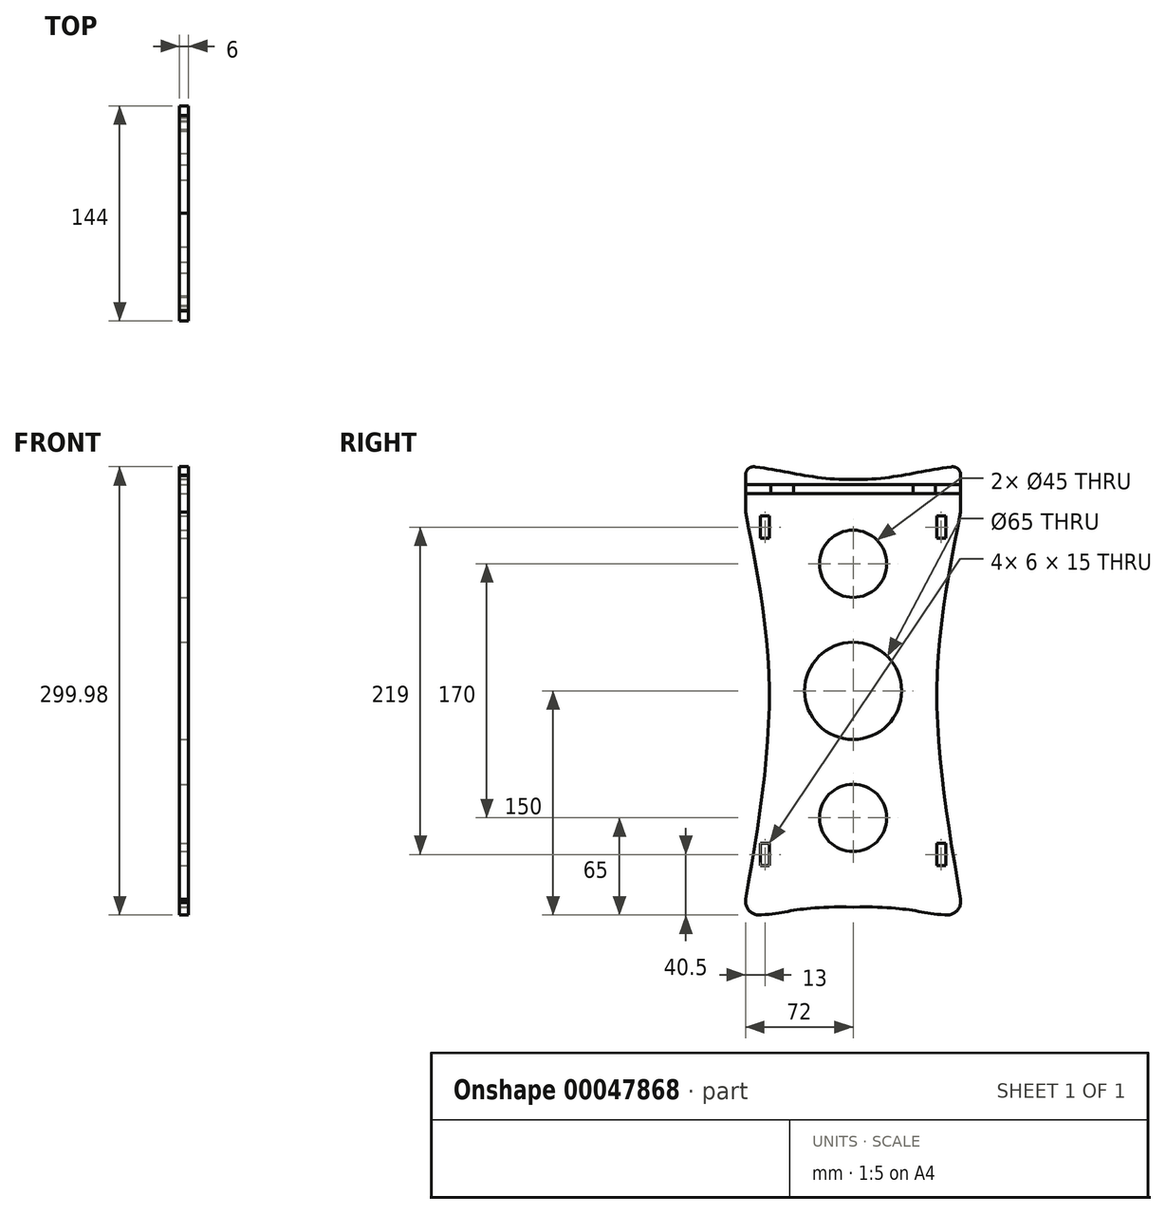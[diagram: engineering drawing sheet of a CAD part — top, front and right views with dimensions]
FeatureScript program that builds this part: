
annotation { "Feature Type Name" : "Feature", "Feature Type Description" : "" }
export const myFeature = defineFeature(function(context is Context, id is Id, definition is map)
    precondition{}
    {
        {
            var Q0;
            Q0=qCreatedBy(makeId("Right.planeOp"),FACE);
            var sketch = newSketch(context, id + "F0", { "sketchPlane" : qUnion([Q0])});
            skLineSegment(sketch, "E0.rect.bottom", {"start": v(-72, 150) * mm, "end": v(72, 150) * mm});
            skLineSegment(sketch, "E0.rect.top", {"start": v(-72, -150) * mm, "end": v(72, -150) * mm});
            skLineSegment(sketch, "E0.rect.left", {"start": v(-72, 150) * mm, "end": v(-72, -150) * mm});
            skLineSegment(sketch, "E0.rect.right", {"start": v(72, 150) * mm, "end": v(72, -150) * mm});
            skPoint(sketch, "E0.rect.middle", {"position": v(0, 0) * mm});
            skSolve(sketch);
        }
        {
            var Q0;
            Q0 = qSketchRegion(id + "F0", true);
            extrude(context, id + "F1", {"entities" : qUnion([Q0]), "depth" : 6 * mm});
        }
        {
            var Q0;
            Q0=makeQuery(id+"F1.opExtrude","CAP_FACE",FACE,{"disambiguationData":[OSD([sQuery(id+"F0.wireOp",EDGE,"E0.rect.bottom"),sQuery(id+"F0.wireOp",EDGE,"E0.rect.top"),sQuery(id+"F0.wireOp",EDGE,"E0.rect.left"),sQuery(id+"F0.wireOp",EDGE,"E0.rect.right")])],"isStart":false});
            var sketch = newSketch(context, id + "F2", { "sketchPlane" : qUnion([Q0])});
            skLineSegment(sketch, "E1", {"start": v(0, 150) * mm, "end": v(0, 138) * mm, "construction": true});
            skLineSegment(sketch, "E2", {"start": v(0, 138) * mm, "end": v(0, 135) * mm});
            skLineSegment(sketch, "E3.rect.bottom", {"start": v(75, 132) * mm, "end": v(-75, 132) * mm});
            skLineSegment(sketch, "E3.rect.top", {"start": v(75, 138) * mm, "end": v(-75, 138) * mm});
            skLineSegment(sketch, "E3.rect.left", {"start": v(75, 132) * mm, "end": v(75, 138) * mm});
            skLineSegment(sketch, "E3.rect.right", {"start": v(-75, 132) * mm, "end": v(-75, 138) * mm});
            skPoint(sketch, "E3.rect.middle", {"position": v(0, 135) * mm});
            skSolve(sketch);
        }
        {
            var Q0;
            Q0 = qSketchRegion(id + "F2", true);
            extrude(context, id + "F3", {"entities" : qUnion([Q0]), "operationType" : NewBodyOperationType.REMOVE, "oppositeDirection" : true, "depth" : 0.1 * mm});
        }
        {
            var Q0;
            {var subQ0=sQuery(id+"F0.wireOp",EDGE,"E0.rect.top");var subQ1=sQuery(id+"F0.wireOp",EDGE,"E0.rect.left");var subQ2=sQuery(id+"F0.wireOp",EDGE,"E0.rect.right");Q0=makeQuery(id+"F3.boolean.opBoolean","SPLIT",FACE,{"disambiguationData":[TD([makeQuery(id+"F1.opExtrude","SWEPT_FACE",FACE,{"disambiguationData":[OSD([subQ0])]})])],"derivedFrom":makeQuery(id+"F1.opExtrude","CAP_FACE",FACE,{"disambiguationData":[OSD([sQuery(id+"F0.wireOp",EDGE,"E0.rect.bottom"),subQ0,subQ1,subQ2])],"isStart":false})});}
            var sketch = newSketch(context, id + "F4", { "sketchPlane" : qUnion([Q0])});
            skArc(sketch, "E4", {"start": v(-72, -139.62) * mm, "mid": v(-69.27, -147.38) * mm, "end": v(-61.48, -150) * mm});
            skPoint(sketch, "E4.first.point", {"position": v(-61.48, -150) * mm});
            skPoint(sketch, "E4.second.point", {"position": v(-72, -139.62) * mm});
            skFitSpline(sketch, "E5", {"points": [v(-72, 119.57) * mm, v(-56.11, 0) * mm, v(-72, -139.62) * mm], "startDerivative": vector(48.35, -243.74) * mm, "endDerivative": vector(-47.13, -274.25) * mm});
            skLineSegment(sketch, "E6", {"start": v(0, -150) * mm, "end": v(0, -144.73) * mm, "construction": true});
            skPoint(sketch, "E6.endSnap0", {"position": v(0, -150) * mm});
            skFitSpline(sketch, "E7", {"points": [v(0, -144.73) * mm, v(-61.48, -150) * mm], "startDerivative": vector(-108.63, 2.12) * mm, "endDerivative": vector(-61.48, -5.27) * mm});
            skLineSegment(sketch, "E8", {"start": v(0, 150.81) * mm, "end": v(0, 141.49) * mm, "construction": true});
            skArc(sketch, "E9", {"start": v(-65.4, 149.82) * mm, "mid": v(-70.1, 148.72) * mm, "end": v(-71.9, 144.26) * mm});
            skLineSegment(sketch, "E10", {"start": v(-72, 119.57) * mm, "end": v(-83.4, 131.88) * mm});
            skLineSegment(sketch, "E11", {"start": v(-83.4, 131.88) * mm, "end": v(-71.9, 144.26) * mm});
            skFitSpline(sketch, "E12", {"points": [v(-65.4, 149.82) * mm, v(0, 141.49) * mm], "startDerivative": vector(66.6, -8.49) * mm, "endDerivative": vector(75.41, 1.56) * mm});
            skFitSpline(sketch, "E13.MirrorCS", {"points": [v(65.4, 149.82) * mm, v(0, 141.49) * mm], "startDerivative": vector(-66.6, -8.49) * mm, "endDerivative": vector(-75.41, 1.56) * mm});
            skArc(sketch, "E14.MirrorCS", {"start": v(65.4, 149.82) * mm, "mid": v(70.1, 148.72) * mm, "end": v(71.9, 144.26) * mm});
            skLineSegment(sketch, "E15.MirrorCS", {"start": v(83.4, 131.88) * mm, "end": v(71.9, 144.26) * mm});
            skLineSegment(sketch, "E16.MirrorCS", {"start": v(72, 119.57) * mm, "end": v(83.4, 131.88) * mm});
            skFitSpline(sketch, "E17.MirrorCS", {"points": [v(72, 119.57) * mm, v(56.11, 0) * mm, v(72, -139.62) * mm], "startDerivative": vector(-48.35, -243.74) * mm, "endDerivative": vector(47.13, -274.25) * mm});
            skArc(sketch, "E18.MirrorCS", {"start": v(72, -139.62) * mm, "mid": v(69.27, -147.38) * mm, "end": v(61.48, -150) * mm});
            skFitSpline(sketch, "E19.MirrorCS", {"points": [v(0, -144.73) * mm, v(61.48, -150) * mm], "startDerivative": vector(108.63, 2.12) * mm, "endDerivative": vector(61.48, -5.27) * mm});
            skLineSegment(sketch, "E20", {"start": v(0, 141.49) * mm, "end": v(0, -144.73) * mm, "construction": true});
            skCircle(sketch, "E21", {"center": v(0, 85) * mm, "radius": 22.5 * mm});
            skCircle(sketch, "E22.MirrorC", {"center": v(0, -85) * mm, "radius": 22.5 * mm});
            skCircle(sketch, "E23", {"center": v(0, 0) * mm, "radius": 32.5 * mm});
            skSolve(sketch);
        }
        {
            var Q0;
            Q0 = qSketchRegion(id + "F4", true);
            extrude(context, id + "F5", {"entities" : qUnion([Q0]), "operationType" : NewBodyOperationType.INTERSECT, "oppositeDirection" : true, "depth" : 25 * mm});
        }
        {
            var Q0;
            Q0=makeQuery(id+"F3.boolean.opBoolean","COPY",FACE,{"derivedFrom":makeQuery(id+"F3.opExtrude","CAP_FACE",FACE,{"disambiguationData":[OSD([sQuery(id+"F2.wireOp",EDGE,"E3.rect.bottom"),sQuery(id+"F2.wireOp",EDGE,"E3.rect.top"),sQuery(id+"F2.wireOp",EDGE,"E3.rect.left"),sQuery(id+"F2.wireOp",EDGE,"E3.rect.right")])],"isStart":false})});
            var sketch = newSketch(context, id + "F6", { "sketchPlane" : qUnion([Q0])});
            skLineSegment(sketch, "E24", {"start": v(0, 132) * mm, "end": v(0, 123.5) * mm, "construction": true});
            skPoint(sketch, "E24.endSnap0", {"position": v(0, 132) * mm});
            skLineSegment(sketch, "E25.bottom", {"start": v(-55, 138) * mm, "end": v(-40, 138) * mm});
            skLineSegment(sketch, "E25.top", {"start": v(-55, 132) * mm, "end": v(-40, 132) * mm});
            skLineSegment(sketch, "E25.left", {"start": v(-55, 138) * mm, "end": v(-55, 132) * mm});
            skLineSegment(sketch, "E25.right", {"start": v(-40, 138) * mm, "end": v(-40, 132) * mm});
            skLineSegment(sketch, "E26.MirrorCS", {"start": v(55, 138) * mm, "end": v(40, 138) * mm});
            skLineSegment(sketch, "E27.MirrorCS", {"start": v(40, 138) * mm, "end": v(40, 132) * mm});
            skLineSegment(sketch, "E28.MirrorCS", {"start": v(55, 132) * mm, "end": v(40, 132) * mm});
            skLineSegment(sketch, "E29.MirrorCS", {"start": v(55, 138) * mm, "end": v(55, 132) * mm});
            skSolve(sketch);
        }
        {
            var Q0;
            Q0 = qSketchRegion(id + "F6", true);
            extrude(context, id + "F7", {"entities" : qUnion([Q0]), "operationType" : NewBodyOperationType.REMOVE, "oppositeDirection" : true, "depth" : 25 * mm});
        }
        {
            var Q0;
            {var subQ0=sQuery(id+"F0.wireOp",EDGE,"E0.rect.top");var subQ1=sQuery(id+"F0.wireOp",EDGE,"E0.rect.left");var subQ2=sQuery(id+"F0.wireOp",EDGE,"E0.rect.right");Q0=makeQuery(id+"F3.boolean.opBoolean","SPLIT",FACE,{"disambiguationData":[TD([makeQuery(id+"F1.opExtrude","SWEPT_FACE",FACE,{"disambiguationData":[OSD([subQ0])]})])],"derivedFrom":makeQuery(id+"F1.opExtrude","CAP_FACE",FACE,{"disambiguationData":[OSD([sQuery(id+"F0.wireOp",EDGE,"E0.rect.bottom"),subQ0,subQ1,subQ2])],"isStart":false})});}
            var sketch = newSketch(context, id + "F8", { "sketchPlane" : qUnion([Q0])});
            skLineSegment(sketch, "E30.bottom", {"start": v(44.43, 137.81) * mm, "end": v(50.43, 137.81) * mm, "construction": true});
            skLineSegment(sketch, "E30.top", {"start": v(44.43, 112.81) * mm, "end": v(50.43, 112.81) * mm, "construction": true});
            skLineSegment(sketch, "E30.left", {"start": v(44.43, 137.81) * mm, "end": v(44.43, 112.81) * mm, "construction": true});
            skLineSegment(sketch, "E30.right", {"start": v(50.43, 137.81) * mm, "end": v(50.43, 112.81) * mm, "construction": true});
            skLineSegment(sketch, "E31.bottom", {"start": v(56, 117) * mm, "end": v(62, 117) * mm});
            skLineSegment(sketch, "E31.top", {"start": v(56, 102) * mm, "end": v(62, 102) * mm});
            skLineSegment(sketch, "E31.left", {"start": v(56, 117) * mm, "end": v(56, 102) * mm});
            skLineSegment(sketch, "E31.right", {"start": v(62, 117) * mm, "end": v(62, 102) * mm});
            skLineSegment(sketch, "E32.MirrorCS", {"start": v(56, -117) * mm, "end": v(56, -102) * mm});
            skLineSegment(sketch, "E33.MirrorCS", {"start": v(56, -117) * mm, "end": v(62, -117) * mm});
            skLineSegment(sketch, "E34.MirrorCS", {"start": v(62, -117) * mm, "end": v(62, -102) * mm});
            skLineSegment(sketch, "E35.MirrorCS", {"start": v(56, -102) * mm, "end": v(62, -102) * mm});
            skLineSegment(sketch, "E36.MirrorCS", {"start": v(-56, 117) * mm, "end": v(-62, 117) * mm});
            skLineSegment(sketch, "E37.MirrorCS", {"start": v(-56, 102) * mm, "end": v(-62, 102) * mm});
            skLineSegment(sketch, "E38.MirrorCS", {"start": v(-56, 117) * mm, "end": v(-56, 102) * mm});
            skLineSegment(sketch, "E39.MirrorCS", {"start": v(-62, 117) * mm, "end": v(-62, 102) * mm});
            skLineSegment(sketch, "E40.MirrorCS", {"start": v(-56, -117) * mm, "end": v(-56, -102) * mm});
            skLineSegment(sketch, "E41.MirrorCS", {"start": v(-56, -117) * mm, "end": v(-62, -117) * mm});
            skLineSegment(sketch, "E42.MirrorCS", {"start": v(-62, -117) * mm, "end": v(-62, -102) * mm});
            skLineSegment(sketch, "E43.MirrorCS", {"start": v(-56, -102) * mm, "end": v(-62, -102) * mm});
            skSolve(sketch);
        }
        {
            var Q0;
            Q0 = qSketchRegion(id + "F8", true);
            extrude(context, id + "F9", {"entities" : qUnion([Q0]), "operationType" : NewBodyOperationType.REMOVE, "oppositeDirection" : true, "depth" : 25 * mm});
        }
    });
